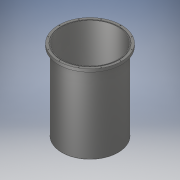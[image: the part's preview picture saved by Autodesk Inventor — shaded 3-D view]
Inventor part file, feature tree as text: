
AUTODESK INVENTOR PART (.ipt)
format: ipt  version: 2018 (Build 220112000, 112)  size: 177,664 bytes
history: native  units: in
note: dims shown in document units (in); Inventor stores cm internally (conversion verified against a paired STEP export)
features: sketch x5, extrude x4, hole x1, pattern_circular x1, fillet x1
ambient origin geometry x8: Origin, YZ Plane, XZ Plane, XY Plane, X Axis, Y Axis, Z Axis, Center Point
bodies: Solid1 (feature_tree)
feature tree (12):
  extrude  "Extrusion1"  Depth=19.125in
  extrude  "Extrusion2"  Depth=1.0in
  hole  "Hole1"  [1 undecoded]
  pattern_circular  "Circular Pattern1"  Count=12 Angle=360.0deg
  extrude  "Extrusion3"  Depth=0.25in
  extrude  "Extrusion6"  Depth=0.25in
  fillet  "Fillet1"  Radius=26.75in
  sketch  "Sketch1"  dims[d0=21.5in d1=19.125in]
  sketch  "Sketch2"  dims[d2=1.0in d3=0.0in d4=19.5in]
  sketch  "Sketch3"  dims[d5=19.875in d6=0.125in d7=0.0in]
  sketch  "Sketch4"  dims[d8=10.4429in]
  sketch  "Sketch8"  dims[d9=0.272in d10=0.63in d11=0.375in d12=0.25in d13=0.5635in d14=0.831in d15=0.8108in d16=4.7244in d17=360.0deg d19=19.125in d20=19.375in d21=26.75in d22=0.0in d45=19.375in d46=0.25in d47=0.0in d48=0.25in]
note: 1 required parameter value undecoded (feature->parameter linkage not recoverable at this tier; creation-order binding heuristic only, values carry confidence <= 0.55)
